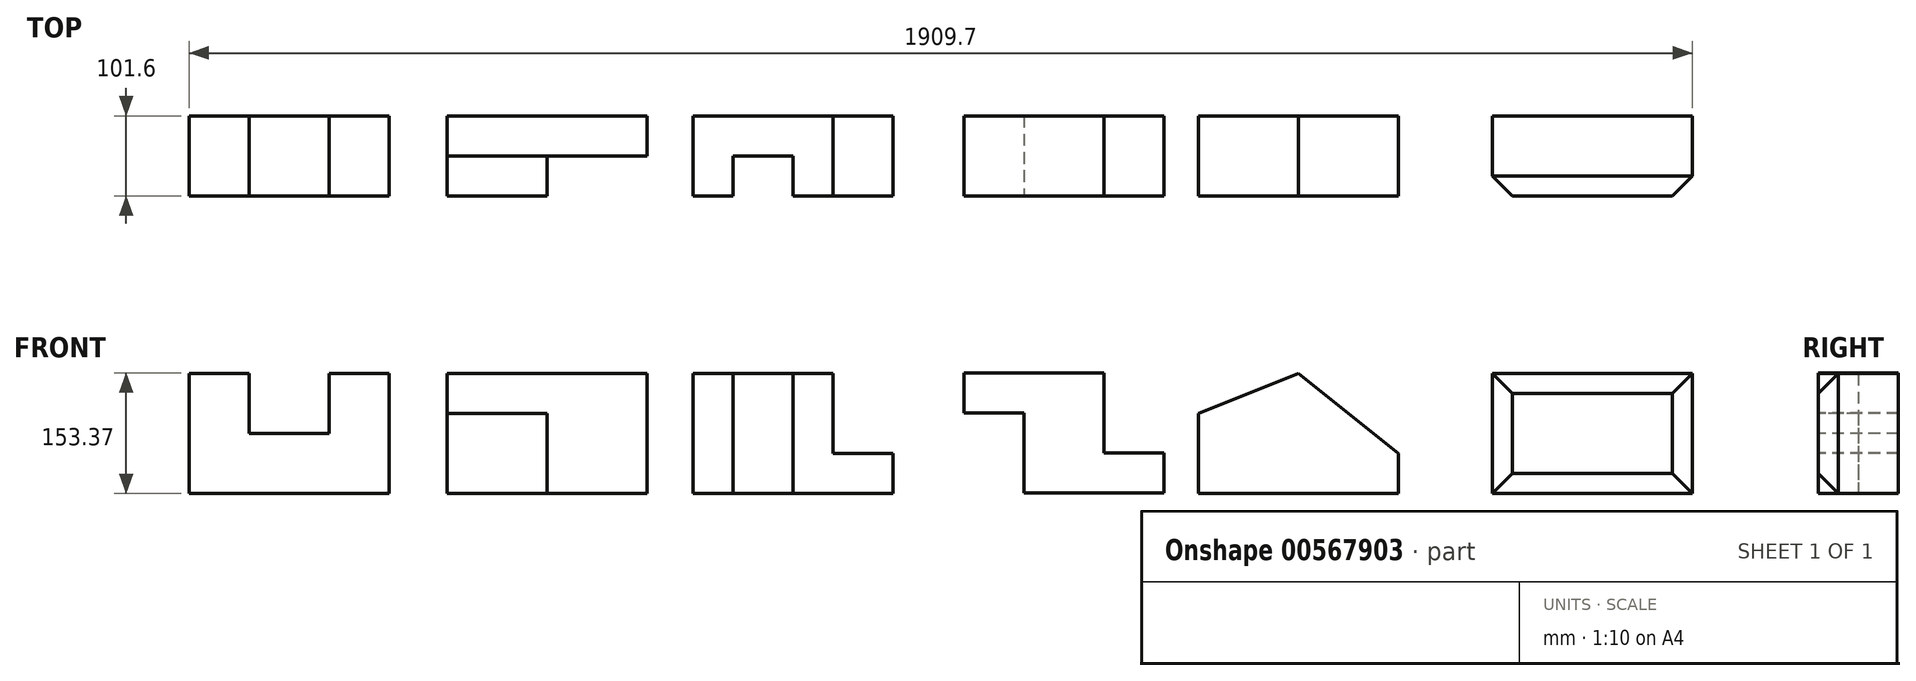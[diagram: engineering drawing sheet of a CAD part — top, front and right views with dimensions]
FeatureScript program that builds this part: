
annotation { "Feature Type Name" : "Feature", "Feature Type Description" : "" }
export const myFeature = defineFeature(function(context is Context, id is Id, definition is map)
    precondition{}
    {
        {
            var Q0;
            Q0=qCreatedBy(makeId("Front.planeOp"),FACE);
            var sketch = newSketch(context, id + "F0", { "sketchPlane" : qUnion([Q0])});
            skLineSegment(sketch, "E0", {"start": v(0, 0) * mm, "end": v(-254, 0) * mm});
            skLineSegment(sketch, "E1", {"start": v(-254, 0) * mm, "end": v(-254, 152.4) * mm});
            skLineSegment(sketch, "E2", {"start": v(-254, 152.4) * mm, "end": v(-177.8, 152.4) * mm});
            skLineSegment(sketch, "E3", {"start": v(-177.8, 152.4) * mm, "end": v(-177.8, 76.2) * mm});
            skLineSegment(sketch, "E4", {"start": v(-177.8, 76.2) * mm, "end": v(-76.2, 76.2) * mm});
            skLineSegment(sketch, "E5", {"start": v(-76.2, 76.2) * mm, "end": v(-76.2, 152.4) * mm});
            skLineSegment(sketch, "E6", {"start": v(-76.2, 152.4) * mm, "end": v(0, 152.4) * mm});
            skLineSegment(sketch, "E7", {"start": v(0, 152.4) * mm, "end": v(0, 0) * mm});
            skSolve(sketch);
        }
        {
            var Q0;
            Q0=makeQuery(id+"F0.imprint","IMPRINT",FACE,{"disambiguationData":[TD([[makeQuery(id+"F0.imprint","IMPRINT",EDGE,{"derivedFrom":sQuery(id+"F0.wireOp",EDGE,"E0")}),-1.0]])]});
            extrude(context, id + "F1", {"entities" : qUnion([Q0]), "oppositeDirection" : true, "depth" : 101.6 * mm, "offsetDistance" : 25.4 * mm});
        }
        {
            var Q0;
            Q0=qCreatedBy(makeId("Top.planeOp"),FACE);
            var sketch = newSketch(context, id + "F2", { "sketchPlane" : qUnion([Q0])});
            skLineSegment(sketch, "E8", {"start": v(73.96, 0) * mm, "end": v(73.96, 101.6) * mm});
            skLineSegment(sketch, "E9", {"start": v(73.96, 101.6) * mm, "end": v(327.96, 101.6) * mm});
            skLineSegment(sketch, "E10", {"start": v(327.96, 101.6) * mm, "end": v(327.96, 50.8) * mm});
            skLineSegment(sketch, "E11", {"start": v(327.96, 50.8) * mm, "end": v(200.96, 50.8) * mm});
            skLineSegment(sketch, "E12", {"start": v(200.96, 50.8) * mm, "end": v(200.96, 0) * mm});
            skLineSegment(sketch, "E13", {"start": v(200.96, 0) * mm, "end": v(73.96, 0) * mm});
            skSolve(sketch);
        }
        {
            var Q0;
            Q0=makeQuery(id+"F2.imprint","IMPRINT",FACE,{"disambiguationData":[TD([[makeQuery(id+"F2.imprint","IMPRINT",EDGE,{"derivedFrom":sQuery(id+"F2.wireOp",EDGE,"E8")}),-1.0]])]});
            extrude(context, id + "F3", {"entities" : qUnion([Q0]), "depth" : 152.4 * mm, "offsetDistance" : 25.4 * mm});
        }
        {
            var Q0;
            Q0=makeQuery(id+"F3.opExtrude","SWEPT_FACE",FACE,{"disambiguationData":[OSD([sQuery(id+"F2.wireOp",EDGE,"E13")])]});
            var sketch = newSketch(context, id + "F4", { "sketchPlane" : qUnion([Q0])});
            skLineSegment(sketch, "E14.bottom", {"start": v(73.96, 152.4) * mm, "end": v(200.96, 152.4) * mm});
            skLineSegment(sketch, "E14.top", {"start": v(73.96, 101.6) * mm, "end": v(200.96, 101.6) * mm});
            skLineSegment(sketch, "E14.left", {"start": v(73.96, 152.4) * mm, "end": v(73.96, 101.6) * mm});
            skLineSegment(sketch, "E14.right", {"start": v(200.96, 152.4) * mm, "end": v(200.96, 101.6) * mm});
            skSolve(sketch);
        }
        {
            var Q0;
            Q0=makeQuery(id+"F4.imprint","IMPRINT",FACE,{"disambiguationData":[TD([[makeQuery(id+"F4.imprint","IMPRINT",EDGE,{"derivedFrom":sQuery(id+"F4.wireOp",EDGE,"E14.bottom")}),1.0]])]});
            extrude(context, id + "F5", {"entities" : qUnion([Q0]), "operationType" : NewBodyOperationType.REMOVE, "oppositeDirection" : true, "depth" : 50.8 * mm, "offsetDistance" : 25.4 * mm});
        }
        {
            var Q0;
            Q0=qCreatedBy(makeId("Top.planeOp"),FACE);
            var sketch = newSketch(context, id + "F6", { "sketchPlane" : qUnion([Q0])});
            skLineSegment(sketch, "E15", {"start": v(386.28, 0) * mm, "end": v(386.28, 101.6) * mm});
            skLineSegment(sketch, "E16", {"start": v(386.28, 101.6) * mm, "end": v(640.28, 101.6) * mm});
            skLineSegment(sketch, "E17", {"start": v(640.28, 101.6) * mm, "end": v(640.28, 0) * mm});
            skLineSegment(sketch, "E18", {"start": v(640.28, 0) * mm, "end": v(513.28, 0) * mm});
            skLineSegment(sketch, "E19", {"start": v(513.28, 0) * mm, "end": v(513.28, 50.8) * mm});
            skLineSegment(sketch, "E20", {"start": v(513.28, 50.8) * mm, "end": v(437.08, 50.8) * mm});
            skLineSegment(sketch, "E21", {"start": v(437.08, 50.8) * mm, "end": v(437.08, 0) * mm});
            skLineSegment(sketch, "E22", {"start": v(437.08, 0) * mm, "end": v(386.28, 0) * mm});
            skSolve(sketch);
        }
        {
            var Q0;
            Q0=makeQuery(id+"F6.imprint","IMPRINT",FACE,{"disambiguationData":[TD([[makeQuery(id+"F6.imprint","IMPRINT",EDGE,{"derivedFrom":sQuery(id+"F6.wireOp",EDGE,"E15")}),-1.0]])]});
            extrude(context, id + "F7", {"entities" : qUnion([Q0]), "depth" : 152.4 * mm, "offsetDistance" : 25.4 * mm});
        }
        {
            var Q0;
            Q0=makeQuery(id+"F7.opExtrude","CAP_FACE",FACE,{"disambiguationData":[OSD([sQuery(id+"F6.wireOp",EDGE,"E15"),sQuery(id+"F6.wireOp",EDGE,"E16"),sQuery(id+"F6.wireOp",EDGE,"E17"),sQuery(id+"F6.wireOp",EDGE,"E18"),sQuery(id+"F6.wireOp",EDGE,"E19"),sQuery(id+"F6.wireOp",EDGE,"E20"),sQuery(id+"F6.wireOp",EDGE,"E21"),sQuery(id+"F6.wireOp",EDGE,"E22")])],"isStart":false});
            var sketch = newSketch(context, id + "F8", { "sketchPlane" : qUnion([Q0])});
            skLineSegment(sketch, "E23.bottom", {"start": v(640.28, 101.6) * mm, "end": v(564.08, 101.6) * mm});
            skLineSegment(sketch, "E23.top", {"start": v(640.28, 0) * mm, "end": v(564.08, 0) * mm});
            skLineSegment(sketch, "E23.left", {"start": v(640.28, 101.6) * mm, "end": v(640.28, 0) * mm});
            skLineSegment(sketch, "E23.right", {"start": v(564.08, 101.6) * mm, "end": v(564.08, 0) * mm});
            skSolve(sketch);
        }
        {
            var Q0;
            Q0=makeQuery(id+"F8.imprint","IMPRINT",FACE,{"disambiguationData":[TD([[makeQuery(id+"F8.imprint","IMPRINT",EDGE,{"derivedFrom":sQuery(id+"F8.wireOp",EDGE,"E23.bottom")}),-1.0]])]});
            extrude(context, id + "F9", {"entities" : qUnion([Q0]), "operationType" : NewBodyOperationType.REMOVE, "oppositeDirection" : true, "depth" : 101.6 * mm, "offsetDistance" : 25.4 * mm});
        }
        {
            var Q0;
            Q0=qCreatedBy(makeId("Front.planeOp"),FACE);
            var sketch = newSketch(context, id + "F10", { "sketchPlane" : qUnion([Q0])});
            skLineSegment(sketch, "E24", {"start": v(806.9, 0.97) * mm, "end": v(806.9, 102.57) * mm});
            skLineSegment(sketch, "E25", {"start": v(806.9, 102.57) * mm, "end": v(730.7, 102.57) * mm});
            skLineSegment(sketch, "E26", {"start": v(730.7, 102.57) * mm, "end": v(730.7, 153.37) * mm});
            skLineSegment(sketch, "E27", {"start": v(730.7, 153.37) * mm, "end": v(908.5, 153.37) * mm});
            skLineSegment(sketch, "E28", {"start": v(908.5, 153.37) * mm, "end": v(908.5, 51.77) * mm});
            skLineSegment(sketch, "E29", {"start": v(908.5, 51.77) * mm, "end": v(984.7, 51.77) * mm});
            skLineSegment(sketch, "E30", {"start": v(984.7, 51.77) * mm, "end": v(984.7, 0.97) * mm});
            skLineSegment(sketch, "E31", {"start": v(984.7, 0.97) * mm, "end": v(806.9, 0.97) * mm});
            skSolve(sketch);
        }
        {
            var Q0;
            Q0=makeQuery(id+"F10.imprint","IMPRINT",FACE,{"disambiguationData":[TD([[makeQuery(id+"F10.imprint","IMPRINT",EDGE,{"derivedFrom":sQuery(id+"F10.wireOp",EDGE,"E24")}),-1.0]])]});
            extrude(context, id + "F11", {"entities" : qUnion([Q0]), "oppositeDirection" : true, "depth" : 101.6 * mm, "offsetDistance" : 25.4 * mm});
        }
        {
            var Q0;
            Q0=qCreatedBy(makeId("Top.planeOp"),FACE);
            var sketch = newSketch(context, id + "F12", { "sketchPlane" : qUnion([Q0])});
            skLineSegment(sketch, "E32", {"start": v(1027.97, 0) * mm, "end": v(1027.97, 101.6) * mm});
            skLineSegment(sketch, "E33", {"start": v(1027.97, 101.6) * mm, "end": v(1281.97, 101.6) * mm});
            skLineSegment(sketch, "E34", {"start": v(1281.97, 101.6) * mm, "end": v(1281.97, 0) * mm});
            skLineSegment(sketch, "E35", {"start": v(1281.97, 0) * mm, "end": v(1027.97, 0) * mm});
            skSolve(sketch);
        }
        {
            var Q0;
            Q0=makeQuery(id+"F12.imprint","IMPRINT",FACE,{"disambiguationData":[TD([[makeQuery(id+"F12.imprint","IMPRINT",EDGE,{"derivedFrom":sQuery(id+"F12.wireOp",EDGE,"E32")}),-1.0]])]});
            extrude(context, id + "F13", {"entities" : qUnion([Q0]), "depth" : 152.4 * mm, "offsetDistance" : 25.4 * mm});
        }
        {
            var Q0;
            Q0=makeQuery(id+"F13.opExtrude","SWEPT_FACE",FACE,{"disambiguationData":[OSD([sQuery(id+"F12.wireOp",EDGE,"E35")])]});
            var sketch = newSketch(context, id + "F14", { "sketchPlane" : qUnion([Q0])});
            skLineSegment(sketch, "E36", {"start": v(1027.97, 152.4) * mm, "end": v(1027.97, 101.6) * mm});
            skLineSegment(sketch, "E37", {"start": v(1027.97, 101.6) * mm, "end": v(1154.97, 152.4) * mm});
            skSolve(sketch);
        }
        {
            var Q0;
            {var subQ0=sQuery(id+"F14.wireOp",EDGE,"E36");Q0=makeQuery(id+"F14.imprint","IMPRINT",FACE,{"disambiguationData":[TD([[makeQuery(id+"F14.imprint","IMPRINT",EDGE,{"derivedFrom":subQ0}),1.0]])]});}
            extrude(context, id + "F15", {"entities" : qUnion([Q0]), "operationType" : NewBodyOperationType.REMOVE, "oppositeDirection" : true, "depth" : 132.08 * mm, "offsetDistance" : 25.4 * mm});
        }
        {
            var Q0;
            Q0=makeQuery(id+"F13.opExtrude","SWEPT_FACE",FACE,{"disambiguationData":[OSD([sQuery(id+"F12.wireOp",EDGE,"E35")])]});
            var sketch = newSketch(context, id + "F16", { "sketchPlane" : qUnion([Q0])});
            skLineSegment(sketch, "E38", {"start": v(1281.97, 0) * mm, "end": v(1281.97, 50.8) * mm});
            skLineSegment(sketch, "E39", {"start": v(1281.97, 50.8) * mm, "end": v(1154.97, 152.4) * mm});
            skSolve(sketch);
        }
        {
            var Q0;
            {var subQ0=sQuery(id+"F16.wireOp",EDGE,"E39");Q0=makeQuery(id+"F16.imprint","IMPRINT",FACE,{"disambiguationData":[TD([[makeQuery(id+"F16.imprint","IMPRINT",EDGE,{"derivedFrom":subQ0}),-1.0]])]});}
            extrude(context, id + "F17", {"entities" : qUnion([Q0]), "operationType" : NewBodyOperationType.REMOVE, "oppositeDirection" : true, "depth" : 152.4 * mm, "offsetDistance" : 25.4 * mm});
        }
        {
            var Q0;
            Q0=qCreatedBy(makeId("Top.planeOp"),FACE);
            var sketch = newSketch(context, id + "F18", { "sketchPlane" : qUnion([Q0])});
            skLineSegment(sketch, "E40", {"start": v(1401.7, 0) * mm, "end": v(1401.7, 101.6) * mm});
            skLineSegment(sketch, "E41", {"start": v(1401.7, 101.6) * mm, "end": v(1655.7, 101.6) * mm});
            skLineSegment(sketch, "E42", {"start": v(1655.7, 101.6) * mm, "end": v(1655.7, 0) * mm});
            skLineSegment(sketch, "E43", {"start": v(1655.7, 0) * mm, "end": v(1401.7, 0) * mm});
            skSolve(sketch);
        }
        {
            var Q0;
            Q0=makeQuery(id+"F18.imprint","IMPRINT",FACE,{"disambiguationData":[TD([[makeQuery(id+"F18.imprint","IMPRINT",EDGE,{"derivedFrom":sQuery(id+"F18.wireOp",EDGE,"E40")}),-1.0]])]});
            extrude(context, id + "F19", {"entities" : qUnion([Q0]), "depth" : 152.4 * mm, "offsetDistance" : 25.4 * mm});
        }
        {
            var Q0;
            Q0=makeQuery(id+"F19.opExtrude","SWEPT_FACE",FACE,{"disambiguationData":[OSD([sQuery(id+"F18.wireOp",EDGE,"E43")])]});
            chamfer(context, id + "F20", {"entities" : qUnion([Q0]), "width" : 25.4 * mm, "tangentPropagation" : true});
        }
    });
